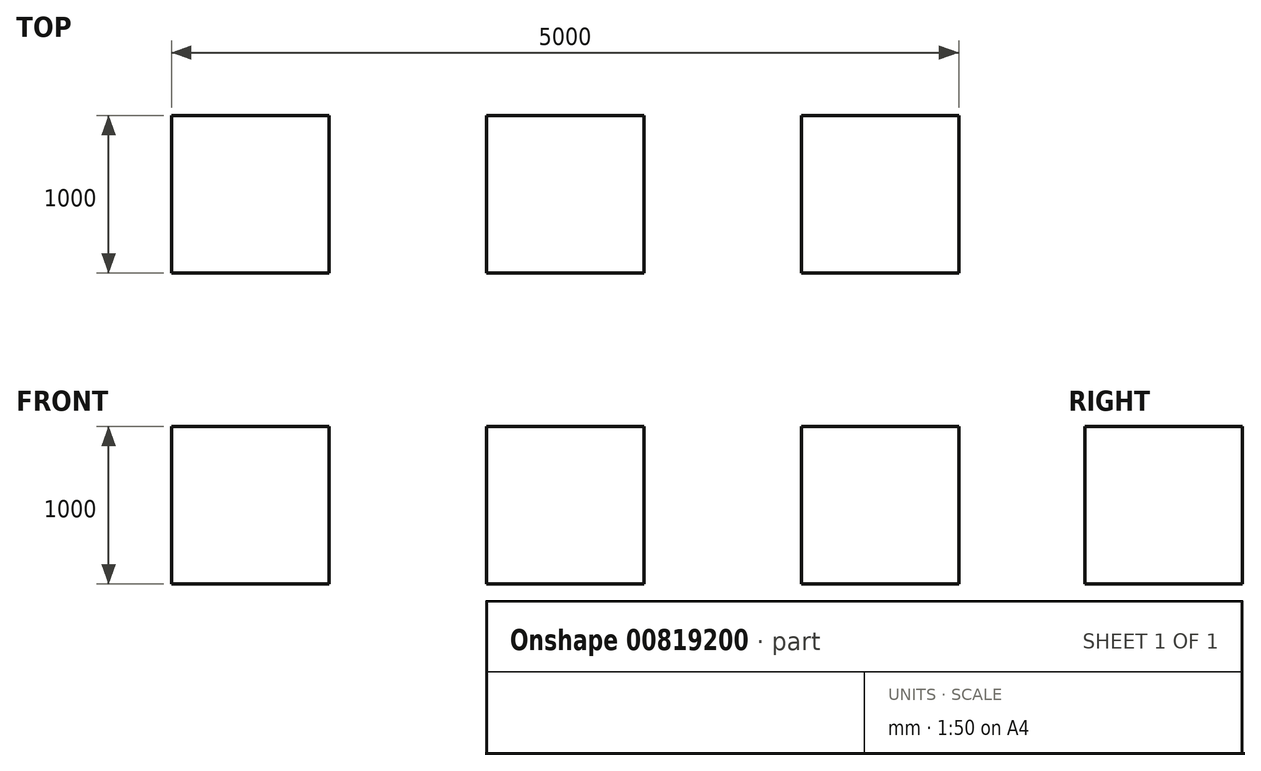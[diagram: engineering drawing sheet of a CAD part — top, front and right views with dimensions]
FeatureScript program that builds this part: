
annotation { "Feature Type Name" : "Feature", "Feature Type Description" : "" }
export const myFeature = defineFeature(function(context is Context, id is Id, definition is map)
    precondition{}
    {
        {
            var Q0;
            Q0=qCreatedBy(makeId("Top.planeOp"),FACE);
            var sketch = newSketch(context, id + "F0", { "sketchPlane" : qUnion([Q0])});
            skLineSegment(sketch, "E0.bottom", {"start": v(500, 500) * mm, "end": v(-500, 500) * mm});
            skLineSegment(sketch, "E0.top", {"start": v(500, -500) * mm, "end": v(-500, -500) * mm});
            skLineSegment(sketch, "E0.left", {"start": v(500, 500) * mm, "end": v(500, -500) * mm});
            skLineSegment(sketch, "E0.right", {"start": v(-500, 500) * mm, "end": v(-500, -500) * mm});
            skPoint(sketch, "E0.middle", {"position": v(0, 0) * mm});
            skSolve(sketch);
        }
        {
            var Q0;
            Q0=qSketchRegion(id+"F0",true);
            extrude(context, id + "F1", {"entities" : qUnion([Q0]), "endBound" : BoundingType.SYMMETRIC, "depth" : 1000 * mm});
        }
        {
            var Q0;
            Q0=makeQuery(id+"F1.opExtrude","SWEPT_BODY",BODY,{"disambiguationData":[OSD([sQuery(id+"F0.wireOp",EDGE,"E0.bottom"),sQuery(id+"F0.wireOp",EDGE,"E0.top"),sQuery(id+"F0.wireOp",EDGE,"E0.left"),sQuery(id+"F0.wireOp",EDGE,"E0.right")])]});
            transform(context, id + "F2", {"entities" : qUnion([Q0]), "transformType" : TransformType.TRANSLATION_3D, "dx" : 2000 * mm, "dy" : 0 * mm, "dz" : 0 * mm, "makeCopy" : true});
        }
        {
            var Q0;
            Q0=makeQuery(id+"F2.opPattern","COPY",BODY,{"derivedFrom":makeQuery(id+"F1.opExtrude","SWEPT_BODY",BODY,{"disambiguationData":[OSD([sQuery(id+"F0.wireOp",EDGE,"E0.bottom"),sQuery(id+"F0.wireOp",EDGE,"E0.top"),sQuery(id+"F0.wireOp",EDGE,"E0.left"),sQuery(id+"F0.wireOp",EDGE,"E0.right")])]}),"instanceName":"1"});
            transform(context, id + "F3", {"entities" : qUnion([Q0]), "transformType" : TransformType.TRANSLATION_3D, "dx" : 2000 * mm, "dy" : 0 * mm, "dz" : 0 * mm, "makeCopy" : true});
        }
    });
